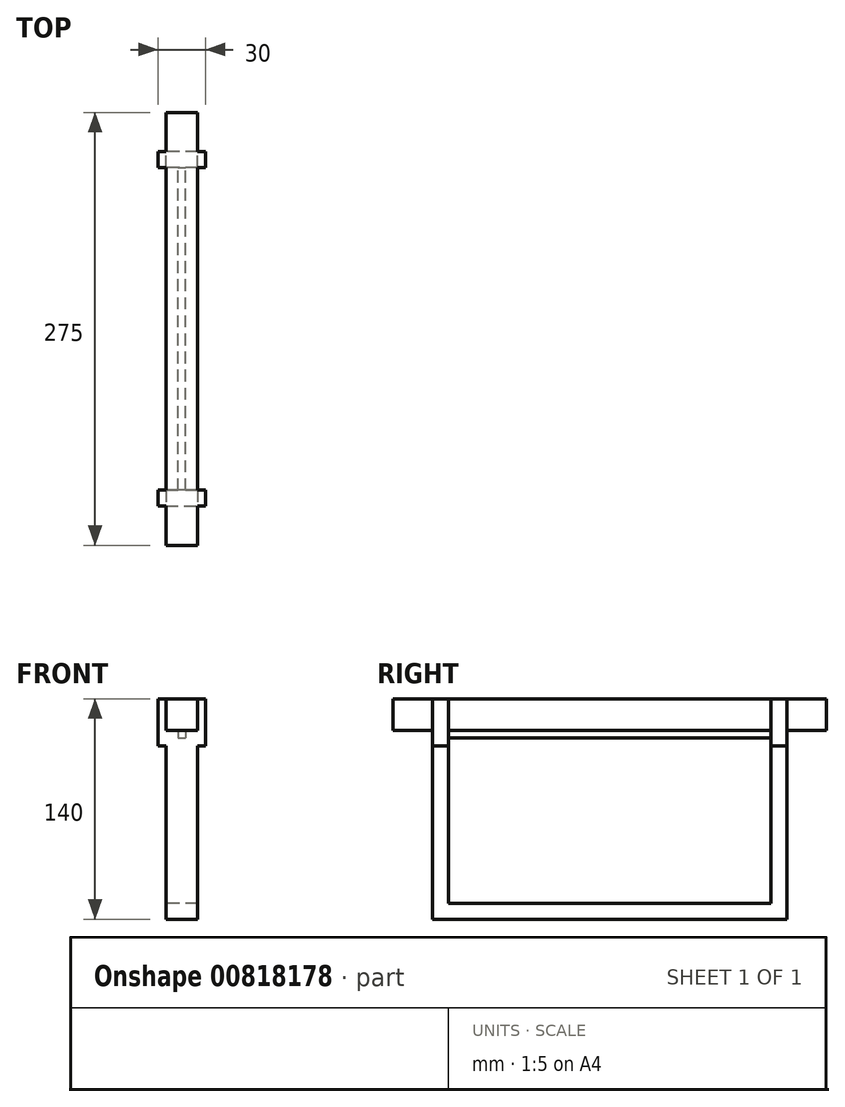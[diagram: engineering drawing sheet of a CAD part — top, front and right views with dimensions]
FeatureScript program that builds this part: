
annotation { "Feature Type Name" : "Feature", "Feature Type Description" : "" }
export const myFeature = defineFeature(function(context is Context, id is Id, definition is map)
    precondition{}
    {
        {
            var Q0;
            Q0=qCreatedBy(makeId("Top.planeOp"),FACE);
            var sketch = newSketch(context, id + "F0", { "sketchPlane" : qUnion([Q0])});
            skLineSegment(sketch, "E0.bottom", {"start": v(10, -137.5) * mm, "end": v(-10, -137.5) * mm});
            skLineSegment(sketch, "E0.top", {"start": v(10, 137.5) * mm, "end": v(-10, 137.5) * mm});
            skLineSegment(sketch, "E0.left", {"start": v(10, -137.5) * mm, "end": v(10, 137.5) * mm});
            skLineSegment(sketch, "E0.right", {"start": v(-10, -137.5) * mm, "end": v(-10, 137.5) * mm});
            skPoint(sketch, "E0.middle", {"position": v(0, 0) * mm});
            skSolve(sketch);
        }
        {
            var Q0;
            Q0=makeQuery(id+"F0.imprint","IMPRINT",FACE,{"disambiguationData":[TD([[makeQuery(id+"F0.imprint","IMPRINT",EDGE,{"derivedFrom":sQuery(id+"F0.wireOp",EDGE,"E0.bottom")}),-1.0]])]});
            extrude(context, id + "F1", {"entities" : qUnion([Q0]), "endBound" : BoundingType.SYMMETRIC, "depth" : 20 * mm, "offsetDistance" : 25 * mm});
        }
        {
            var Q0;
            Q0=makeQuery(id+"F1.opExtrude","SWEPT_FACE",FACE,{"disambiguationData":[OSD([sQuery(id+"F0.wireOp",EDGE,"E0.bottom")])]});
            cPlane(context, id + "F2", {"entities" : qUnion([Q0]), "cplaneType" : CPlaneType.OFFSET, "offset" : 25 * mm, "oppositeDirection" : true, "width" : 150 * mm, "height" : 150 * mm});
        }
        {
            var Q0;
            Q0=qCreatedBy(id+"F2.planeOp",FACE);
            var sketch = newSketch(context, id + "F3", { "sketchPlane" : qUnion([Q0])});
            skLineSegment(sketch, "E1.top", {"start": v(15, 10) * mm, "end": v(-15, 10) * mm});
            skPoint(sketch, "E1.middle", {"position": v(0, 0) * mm});
            skLineSegment(sketch, "E2.bottom", {"start": v(-10, 0) * mm, "end": v(10, 0) * mm});
            skLineSegment(sketch, "E2.top", {"start": v(-10, -130) * mm, "end": v(10, -130) * mm});
            skLineSegment(sketch, "E2.left", {"start": v(-10, 0) * mm, "end": v(-10, -130) * mm});
            skLineSegment(sketch, "E2.right", {"start": v(10, 0) * mm, "end": v(10, -130) * mm});
            skLineSegment(sketch, "E3", {"start": v(-15, 10) * mm, "end": v(-15, -20) * mm});
            skLineSegment(sketch, "E4", {"start": v(-15, -20) * mm, "end": v(15, -20) * mm});
            skLineSegment(sketch, "E5", {"start": v(15, -20) * mm, "end": v(15, 10) * mm});
            skSolve(sketch);
        }
        {
            var Q0;
            {var subQ5=sQuery(id+"F3.wireOp",EDGE,"E2.top");Q0=makeQuery(id+"F3.imprint","IMPRINT",FACE,{"disambiguationData":[TD([[makeQuery(id+"F3.imprint","IMPRINT",EDGE,{"derivedFrom":subQ5}),1.0]])]});}
            var Q1;
            {var subQ5=sQuery(id+"F3.wireOp",EDGE,"E2.bottom");Q1=makeQuery(id+"F3.imprint","IMPRINT",FACE,{"disambiguationData":[TD([[makeQuery(id+"F3.imprint","IMPRINT",EDGE,{"derivedFrom":subQ5}),-1.0]])]});}
            var Q2;
            Q2=makeQuery(id+"F3.imprint","IMPRINT",FACE,{"disambiguationData":[TD([[makeQuery(id+"F3.imprint","IMPRINT",EDGE,{"derivedFrom":sQuery(id+"F3.wireOp",EDGE,"E1.top")}),1.0]])]});
            extrude(context, id + "F4", {"entities" : qUnion([Q0, Q1, Q2]), "operationType" : NewBodyOperationType.ADD, "oppositeDirection" : true, "depth" : 10 * mm, "offsetDistance" : 25 * mm});
        }
        {
            var Q0;
            Q0=makeQuery(id+"F1.opExtrude","SWEPT_FACE",FACE,{"disambiguationData":[OSD([sQuery(id+"F0.wireOp",EDGE,"E0.top")])]});
            cPlane(context, id + "F5", {"entities" : qUnion([Q0]), "cplaneType" : CPlaneType.OFFSET, "offset" : 25 * mm, "oppositeDirection" : true, "width" : 150 * mm, "height" : 150 * mm});
        }
        {
            var Q0;
            Q0=qCreatedBy(id+"F5.planeOp",FACE);
            var sketch = newSketch(context, id + "F6", { "sketchPlane" : qUnion([Q0])});
            skLineSegment(sketch, "E6.top", {"start": v(15, 10) * mm, "end": v(-15, 10) * mm});
            skPoint(sketch, "E6.middle", {"position": v(0, 0) * mm});
            skLineSegment(sketch, "E7.bottom", {"start": v(-10, 0) * mm, "end": v(10, 0) * mm});
            skLineSegment(sketch, "E7.top", {"start": v(-10, -130) * mm, "end": v(10, -130) * mm});
            skLineSegment(sketch, "E7.left", {"start": v(-10, 0) * mm, "end": v(-10, -130) * mm});
            skLineSegment(sketch, "E7.right", {"start": v(10, 0) * mm, "end": v(10, -130) * mm});
            skLineSegment(sketch, "E8", {"start": v(-15, 10) * mm, "end": v(-15, -20) * mm});
            skLineSegment(sketch, "E9", {"start": v(-15, -20) * mm, "end": v(15, -20) * mm});
            skLineSegment(sketch, "E10", {"start": v(15, -20) * mm, "end": v(15, 10) * mm});
            skSolve(sketch);
        }
        {
            var Q0;
            {var subQ5=sQuery(id+"F6.wireOp",EDGE,"E7.bottom");Q0=makeQuery(id+"F6.imprint","IMPRINT",FACE,{"disambiguationData":[TD([[makeQuery(id+"F6.imprint","IMPRINT",EDGE,{"derivedFrom":subQ5}),-1.0]])]});}
            var Q1;
            {var subQ5=sQuery(id+"F6.wireOp",EDGE,"E7.top");Q1=makeQuery(id+"F6.imprint","IMPRINT",FACE,{"disambiguationData":[TD([[makeQuery(id+"F6.imprint","IMPRINT",EDGE,{"derivedFrom":subQ5}),1.0]])]});}
            var Q2;
            Q2=makeQuery(id+"F6.imprint","IMPRINT",FACE,{"disambiguationData":[TD([[makeQuery(id+"F6.imprint","IMPRINT",EDGE,{"derivedFrom":sQuery(id+"F6.wireOp",EDGE,"E6.top")}),1.0]])]});
            extrude(context, id + "F7", {"entities" : qUnion([Q0, Q1, Q2]), "operationType" : NewBodyOperationType.ADD, "oppositeDirection" : true, "depth" : 10 * mm, "offsetDistance" : 25 * mm});
        }
        {
            var Q0;
            Q0=makeQuery(id+"F7.opExtrude","SWEPT_FACE",FACE,{"disambiguationData":[OSD([sQuery(id+"F6.wireOp",EDGE,"E7.top")])]});
            var sketch = newSketch(context, id + "F8", { "sketchPlane" : qUnion([Q0])});
            skLineSegment(sketch, "E11.bottom", {"start": v(10, -102.5) * mm, "end": v(-10, -102.5) * mm});
            skLineSegment(sketch, "E11.top", {"start": v(10, 102.5) * mm, "end": v(-10, 102.5) * mm});
            skLineSegment(sketch, "E11.left", {"start": v(10, -102.5) * mm, "end": v(10, 102.5) * mm});
            skLineSegment(sketch, "E11.right", {"start": v(-10, -102.5) * mm, "end": v(-10, 102.5) * mm});
            skSolve(sketch);
        }
        {
            var Q0;
            Q0=makeQuery(id+"F8.imprint","IMPRINT",FACE,{"disambiguationData":[TD([[makeQuery(id+"F8.imprint","IMPRINT",EDGE,{"derivedFrom":sQuery(id+"F8.wireOp",EDGE,"E11.bottom")}),-1.0]])]});
            extrude(context, id + "F9", {"entities" : qUnion([Q0]), "operationType" : NewBodyOperationType.ADD, "oppositeDirection" : true, "depth" : 10 * mm, "offsetDistance" : 25 * mm});
        }
        {
            var Q0;
            Q0=qCreatedBy(makeId("Top.planeOp"),FACE);
            var sketch = newSketch(context, id + "F10", { "sketchPlane" : qUnion([Q0])});
            skLineSegment(sketch, "E12.bottom", {"start": v(2.5, -110) * mm, "end": v(-2.5, -110) * mm});
            skLineSegment(sketch, "E12.top", {"start": v(2.5, 110) * mm, "end": v(-2.5, 110) * mm});
            skLineSegment(sketch, "E12.left", {"start": v(2.5, -110) * mm, "end": v(2.5, 110) * mm});
            skLineSegment(sketch, "E12.right", {"start": v(-2.5, -110) * mm, "end": v(-2.5, 110) * mm});
            skPoint(sketch, "E12.middle", {"position": v(0, 0) * mm});
            skSolve(sketch);
        }
        {
            var Q0;
            Q0 = qSketchRegion(id + "F10", true);
            extrude(context, id + "F11", {"entities" : qUnion([Q0]), "operationType" : NewBodyOperationType.ADD, "oppositeDirection" : true, "depth" : 15 * mm, "offsetDistance" : 25 * mm});
        }
    });
